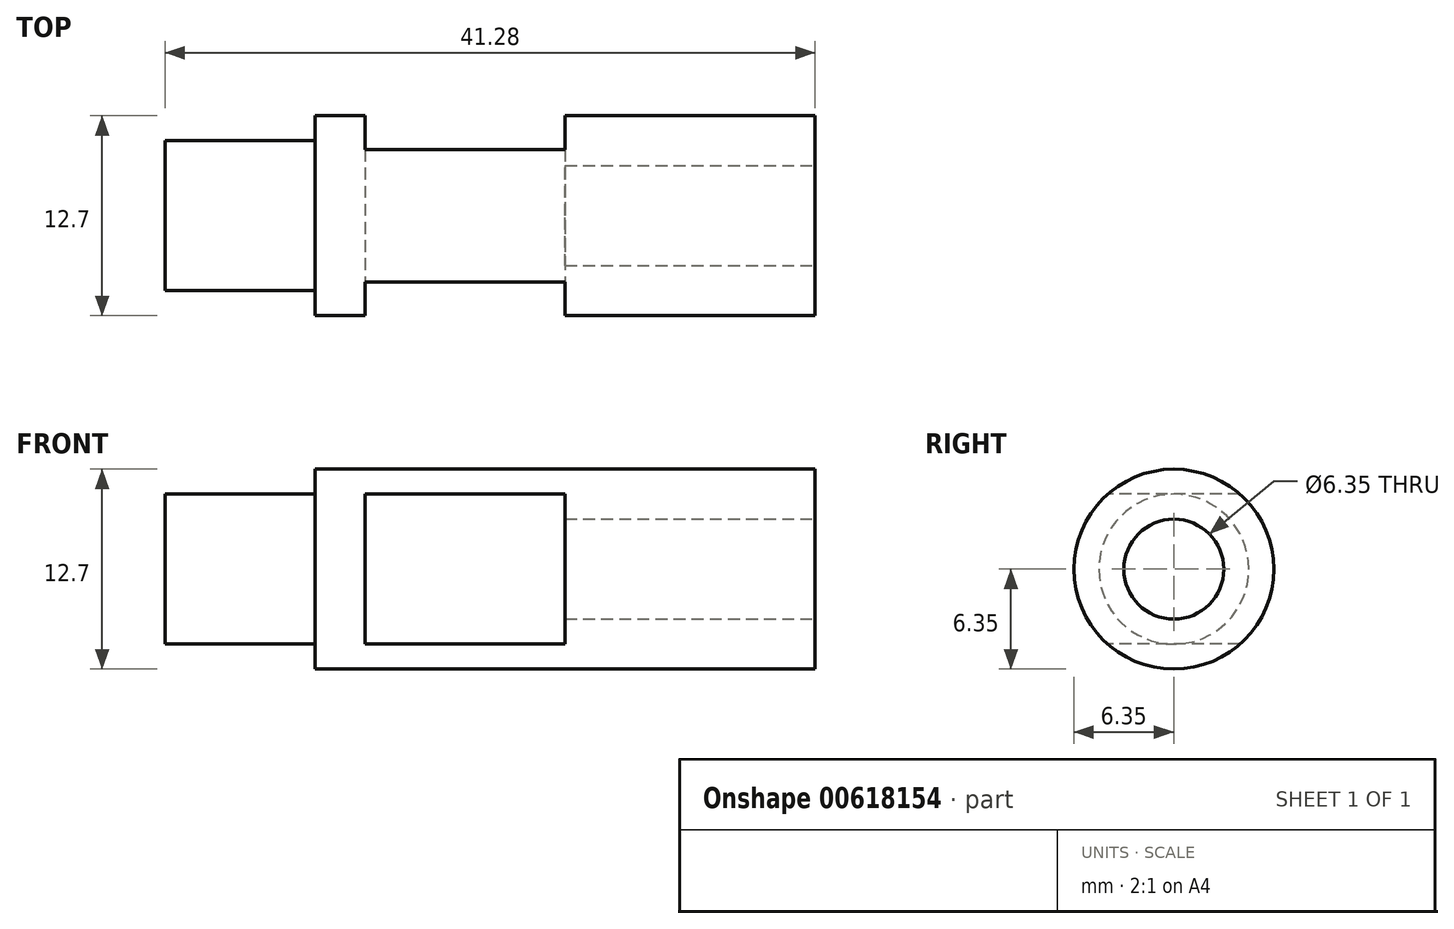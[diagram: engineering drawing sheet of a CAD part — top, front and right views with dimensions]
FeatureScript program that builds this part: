
annotation { "Feature Type Name" : "Feature", "Feature Type Description" : "" }
export const myFeature = defineFeature(function(context is Context, id is Id, definition is map)
    precondition{}
    {
        {
            var Q0;
            Q0=qCreatedBy(makeId("Front.planeOp"),FACE);
            var sketch = newSketch(context, id + "F0", { "sketchPlane" : qUnion([Q0])});
            skLineSegment(sketch, "E0", {"start": v(0, 0) * mm, "end": v(0, 4.76) * mm});
            skLineSegment(sketch, "E1", {"start": v(0, 4.76) * mm, "end": v(9.53, 4.76) * mm});
            skLineSegment(sketch, "E2", {"start": v(9.53, 4.76) * mm, "end": v(9.53, 6.35) * mm});
            skLineSegment(sketch, "E3", {"start": v(9.53, 6.35) * mm, "end": v(41.27, 6.35) * mm});
            skLineSegment(sketch, "E4", {"start": v(41.27, 6.35) * mm, "end": v(41.27, 3.18) * mm});
            skLineSegment(sketch, "E5", {"start": v(41.27, 3.18) * mm, "end": v(22.23, 3.18) * mm});
            skLineSegment(sketch, "E6", {"start": v(22.23, 3.18) * mm, "end": v(22.23, 0) * mm});
            skLineSegment(sketch, "E7", {"start": v(22.23, 0) * mm, "end": v(0, 0) * mm});
            skSolve(sketch);
        }
        {
            var Q0;
            Q0=makeQuery(id+"F0.imprint","IMPRINT",FACE,{"disambiguationData":[TD([[makeQuery(id+"F0.imprint","IMPRINT",EDGE,{"derivedFrom":sQuery(id+"F0.wireOp",EDGE,"E0")}),-1.0]])]});
            var Q1;
            Q1=sQuery(id+"F0.wireOp",EDGE,"E7");
            revolve(context, id + "F1", {"entities" : qUnion([Q0]), "axis" : qUnion([Q1]), "revolveType" : RevolveType.FULL});
        }
        {
            var Q0;
            Q0=qCreatedBy(makeId("Front.planeOp"),FACE);
            var sketch = newSketch(context, id + "F2", { "sketchPlane" : qUnion([Q0])});
            skLineSegment(sketch, "E8", {"start": v(0, 0) * mm, "end": v(41.28, 0) * mm});
            skLineSegment(sketch, "E9.bottom", {"start": v(25.4, -4.76) * mm, "end": v(12.7, -4.76) * mm});
            skLineSegment(sketch, "E9.top", {"start": v(25.4, 4.76) * mm, "end": v(12.7, 4.76) * mm});
            skLineSegment(sketch, "E9.left", {"start": v(25.4, -4.76) * mm, "end": v(25.4, 4.76) * mm});
            skLineSegment(sketch, "E9.right", {"start": v(12.7, -4.76) * mm, "end": v(12.7, 4.76) * mm});
            skPoint(sketch, "E9.middle", {"position": v(19.05, 0) * mm});
            skLineSegment(sketch, "E10", {"start": v(9.53, 4.76) * mm, "end": v(9.53, 6.35) * mm});
            skLineSegment(sketch, "E11", {"start": v(9.53, -6.35) * mm, "end": v(9.53, -4.76) * mm});
            skSolve(sketch);
        }
        {
            var Q0;
            Q0=qSketchRegion(id+"F2",true);
            extrude(context, id + "F3", {"entities" : qUnion([Q0]), "operationType" : NewBodyOperationType.REMOVE, "endBound" : BoundingType.THROUGH_ALL, "oppositeDirection" : true, "depth" : 25.4 * mm, "hasSecondDirection" : true, "secondDirectionBound" : SecondDirectionBoundingType.THROUGH_ALL, "secondDirectionOppositeDirection" : false, "secondDirectionDepth" : 25.4 * mm});
        }
    });
